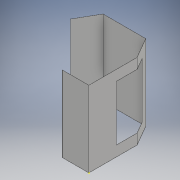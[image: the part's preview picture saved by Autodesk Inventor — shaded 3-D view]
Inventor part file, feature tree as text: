
AUTODESK INVENTOR PART (.ipt)
format: ipt  version: 2018 (Build 220112000, 112)  size: 132,608 bytes
history: native  units: mm
features: sketch x4, extrude x3
ambient origin geometry x8: Origin, YZ Plane, XZ Plane, XY Plane, X Axis, Y Axis, Z Axis, Center Point
bodies: Solid1 (feature_tree)
feature tree (7):
  extrude  "Extrusion1"  Depth=700.0mm
  sketch  "Sketch2"  dims[d2=90.0deg d3=346.0mm]
  sketch  "Sketch3"  dims[d4=150.0deg d5=620.0mm]
  extrude  "Extrusion2"  Depth=346.0mm
  extrude  "Extrusion3"  Depth=620.0mm
  sketch  "Sketch1"  dims[d0=385.0mm d1=700.0mm]
  sketch  "Sketch4"  dims[d6=346.0mm d7=120.0deg d8=1.6mm d9=1100.0mm d10=0.0mm d13=800.0mm d14=300.0mm d16=800.0mm d17=200.0mm d18=1.6mm d19=0.0mm d20=1.6mm d21=0.0mm]
